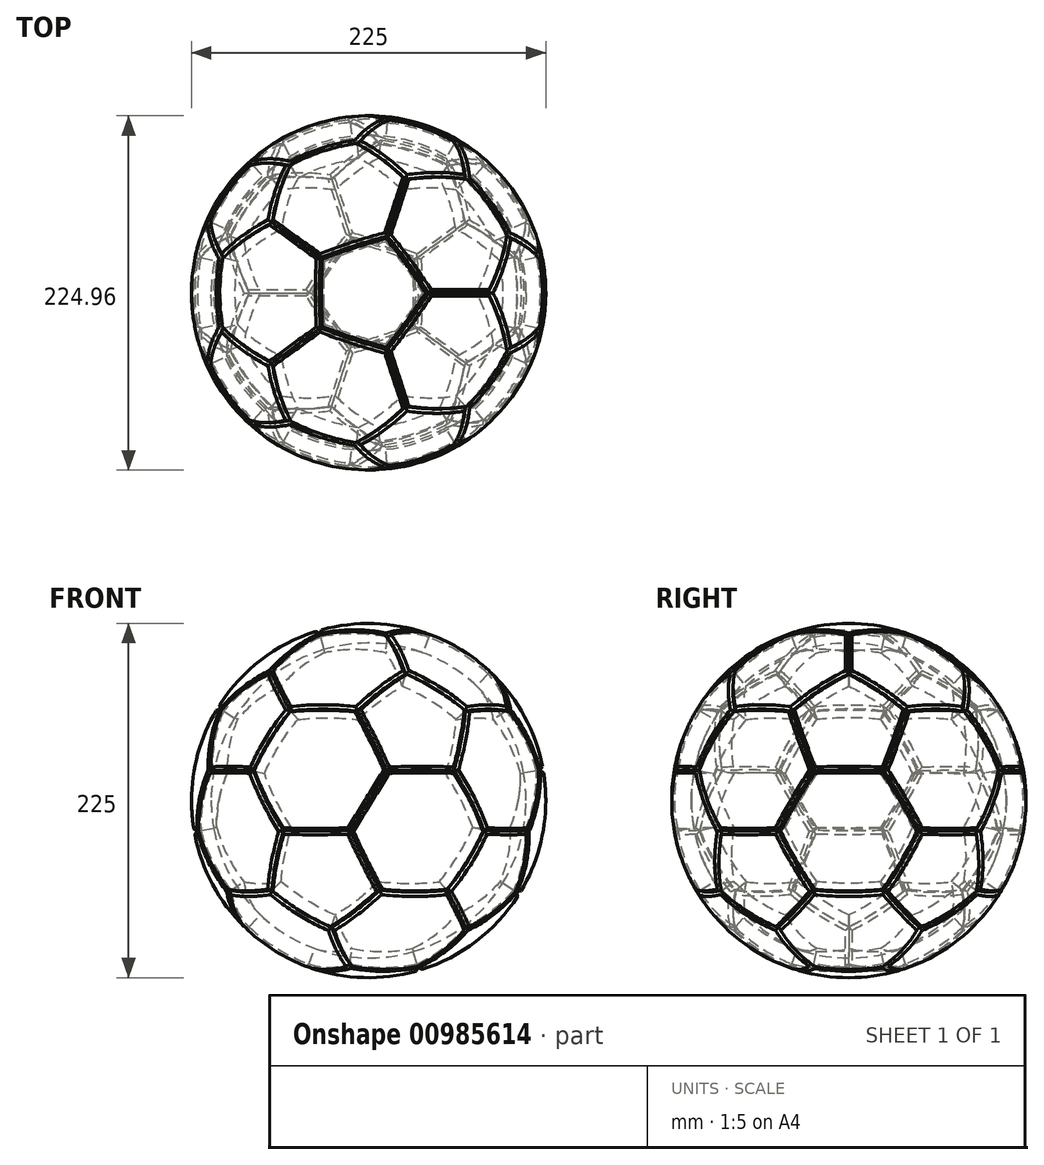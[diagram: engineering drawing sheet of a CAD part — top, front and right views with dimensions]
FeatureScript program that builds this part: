
annotation { "Feature Type Name" : "Feature", "Feature Type Description" : "" }
export const myFeature = defineFeature(function(context is Context, id is Id, definition is map)
    precondition{}
    {
        {
            var Q0;
            Q0=qCreatedBy(makeId("Top.planeOp"),FACE);
            var sketch = newSketch(context, id + "F0", { "sketchPlane" : qUnion([Q0])});
            skLineSegment(sketch, "E0.0", {"start": v(-13.14, 40.45) * mm, "end": v(34.4, 25) * mm});
            skLineSegment(sketch, "E0.1", {"start": v(34.4, 25) * mm, "end": v(34.4, -25) * mm});
            skLineSegment(sketch, "E0.2", {"start": v(34.4, -25) * mm, "end": v(-13.14, -40.45) * mm});
            skLineSegment(sketch, "E0.3", {"start": v(-13.14, -40.45) * mm, "end": v(-42.53, 0) * mm});
            skLineSegment(sketch, "E0.4", {"start": v(-42.53, 0) * mm, "end": v(-13.14, 40.45) * mm});
            skLineSegment(sketch, "E1", {"start": v(34.4, -25) * mm, "end": v(34.4, -50) * mm, "construction": true});
            skLineSegment(sketch, "E2", {"start": v(77.71, -50) * mm, "end": v(34.4, -50) * mm, "construction": true});
            skLineSegment(sketch, "E3", {"start": v(34.4, -25) * mm, "end": v(-27.84, 20.23) * mm, "construction": true});
            skLineSegment(sketch, "E4.MirrorCS", {"start": v(34.4, -25) * mm, "end": v(58.19, -17.27) * mm, "construction": true});
            skLineSegment(sketch, "E5.MirrorCS", {"start": v(71.57, -58.46) * mm, "end": v(58.19, -17.27) * mm, "construction": true});
            skSolve(sketch);
        }
        {
            var Q0;
            Q0=sQuery(id+"F0.wireOp",VERTEX,"E1.end");
            var Q1;
            Q1=sQuery(id+"F0.wireOp",EDGE,"E1");
            cPlane(context, id + "F1", {"entities" : qUnion([Q0, Q1]), "cplaneType" : CPlaneType.LINE_POINT, "offset" : 25 * mm, "width" : 150 * mm, "height" : 150 * mm});
        }
        {
            var Q0;
            Q0=qCreatedBy(id+"F1.planeOp",FACE);
            var sketch = newSketch(context, id + "F2", { "sketchPlane" : qUnion([Q0])});
            skCircle(sketch, "E6", {"center": v(34.4, 0) * mm, "radius": 43.3 * mm});
            skSolve(sketch);
        }
        {
            var Q0;
            Q0=sQuery(id+"F0.wireOp",VERTEX,"E4.MirrorCS.end");
            var Q1;
            Q1=sQuery(id+"F0.wireOp",EDGE,"E4.MirrorCS");
            cPlane(context, id + "F3", {"entities" : qUnion([Q0, Q1]), "cplaneType" : CPlaneType.LINE_POINT, "offset" : 25 * mm, "width" : 150 * mm, "height" : 150 * mm});
        }
        {
            var Q0;
            Q0=qCreatedBy(id+"F3.planeOp",FACE);
            var sketch = newSketch(context, id + "F4", { "sketchPlane" : qUnion([Q0])});
            skCircle(sketch, "E7", {"center": v(-34.4, 0) * mm, "radius": 43.3 * mm});
            skSolve(sketch);
        }
        {
            var Q0;
            Q0=makeQuery(id+"F2.imprint","IMPRINT",FACE,{"disambiguationData":[TD([[makeQuery(id+"F2.imprint","IMPRINT",EDGE,{"derivedFrom":sQuery(id+"F2.wireOp",EDGE,"E6")}),1.0]])]});
            extrude(context, id + "F5", {"entities" : qUnion([Q0]), "depth" : 25 * mm, "offsetDistance" : 25 * mm});
        }
        {
            var Q0;
            Q0=makeQuery(id+"F4.imprint","IMPRINT",FACE,{"disambiguationData":[TD([[makeQuery(id+"F4.imprint","IMPRINT",EDGE,{"derivedFrom":sQuery(id+"F4.wireOp",EDGE,"E7")}),1.0]])]});
            extrude(context, id + "F6", {"entities" : qUnion([Q0]), "depth" : 25 * mm, "offsetDistance" : 25 * mm});
        }
        {
            var Q0;
            Q0=makeQuery(id+"F5.opExtrude","SWEPT_BODY",BODY,{"disambiguationData":[OSD([sQuery(id+"F2.wireOp",EDGE,"E6")])]});
            var Q1;
            Q1=makeQuery(id+"F6.opExtrude","SWEPT_BODY",BODY,{"disambiguationData":[OSD([sQuery(id+"F4.wireOp",EDGE,"E7")])]});
            booleanBodies(context, id + "F7", {"operationType" : BooleanOperationType.INTERSECTION, "tools" : qUnion([Q0, Q1])});
        }
        {
            var Q0;
            Q0=sQuery(id+"F0.wireOp",VERTEX,"E0.0.end");
            var Q1;
            Q1=sQuery(id+"F0.wireOp",VERTEX,"E0.1.end");
            var Q2;
            {var subQ0=sQuery(id+"F4.wireOp",EDGE,"E7");var subQ1=sQuery(id+"F2.wireOp",EDGE,"E6");Q2=makeQuery(id+"F7.opBoolean","INTERSECT",VERTEX,{"disambiguationData":[OD(1.0)],"derivedFrom":[makeQuery(id+"F5.opExtrude","SWEPT_FACE",FACE,{"disambiguationData":[OSD([subQ1])]}),makeQuery(id+"F5.opExtrude","CAP_FACE",FACE,{"disambiguationData":[OSD([subQ1])],"isStart":true}),makeQuery(id+"F6.opExtrude","SWEPT_FACE",FACE,{"disambiguationData":[OSD([subQ0])]}),makeQuery(id+"F6.opExtrude","CAP_FACE",FACE,{"disambiguationData":[OSD([subQ0])],"isStart":true})]});}
            cPlane(context, id + "F8", {"entities" : qUnion([Q0, Q1, Q2]), "cplaneType" : CPlaneType.THREE_POINT, "offset" : 25 * mm, "width" : 150 * mm, "height" : 150 * mm});
        }
        {
            var Q0;
            Q0=qCreatedBy(id+"F8.planeOp",FACE);
            var sketch = newSketch(context, id + "F9", { "sketchPlane" : qUnion([Q0])});
            skLineSegment(sketch, "E8.0", {"start": v(113.95, 25) * mm, "end": v(113.95, -25) * mm});
            skLineSegment(sketch, "E8.1", {"start": v(113.95, -25) * mm, "end": v(70.64, -50) * mm});
            skLineSegment(sketch, "E8.2", {"start": v(70.64, -50) * mm, "end": v(27.34, -25) * mm});
            skLineSegment(sketch, "E8.3", {"start": v(27.34, -25) * mm, "end": v(27.34, 25) * mm});
            skLineSegment(sketch, "E8.4", {"start": v(27.34, 25) * mm, "end": v(70.64, 50) * mm});
            skLineSegment(sketch, "E8.5", {"start": v(70.64, 50) * mm, "end": v(113.95, 25) * mm});
            skLineSegment(sketch, "E9", {"start": v(70.64, 0) * mm, "end": v(27.34, -25) * mm, "construction": true});
            skSolve(sketch);
        }
        {
            var Q0;
            Q0=qCreatedBy(makeId("Front.planeOp"),FACE);
            var sketch = newSketch(context, id + "F10", { "sketchPlane" : qUnion([Q0])});
            skLineSegment(sketch, "E10", {"start": v(0, 0) * mm, "end": v(0, 116.37) * mm, "construction": true});
            skLineSegment(sketch, "E11", {"start": v(68.82, 26.29) * mm, "end": v(0, 116.37) * mm, "construction": true});
            skSolve(sketch);
        }
        {
            var Q0;
            Q0=makeQuery(id+"F0.imprint","IMPRINT",FACE,{"disambiguationData":[TD([[makeQuery(id+"F0.imprint","IMPRINT",EDGE,{"derivedFrom":sQuery(id+"F0.wireOp",EDGE,"E0.0")}),-1.0]])]});
            var Q1;
            Q1=sQuery(id+"F10.wireOp",VERTEX,"E10.end");
            loft(context, id + "F11", {"sheetProfilesArray" : [{ "sheetProfileEntities" : qUnion([Q0]) }, { "sheetProfileEntities" : qUnion([Q1]) }]});
        }
        {
            var Q1;
            Q1=makeQuery(id+"F9.imprint","IMPRINT",FACE,{"disambiguationData":[TD([[makeQuery(id+"F9.imprint","IMPRINT",EDGE,{"derivedFrom":sQuery(id+"F9.wireOp",EDGE,"E8.0")}),-1.0]])]});
            var Q2;
            Q2=sQuery(id+"F10.wireOp",VERTEX,"E10.end");
            loft(context, id + "F12", {"sheetProfilesArray" : [{ "sheetProfileEntities" : qUnion([Q1]) }, { "sheetProfileEntities" : qUnion([Q2]) }]});
        }
        {
            var Q0;
            Q0=makeQuery(id+"F12.opLoft","SWEPT_BODY",BODY,{"disambiguationData":[OSD([makeQuery(id+"F9.imprint","IMPRINT",FACE,{"disambiguationData":[TD([[makeQuery(id+"F9.imprint","IMPRINT",EDGE,{"derivedFrom":sQuery(id+"F9.wireOp",EDGE,"E8.0")}),-1.0]])]}),sQuery(id+"F10.wireOp",VERTEX,"E10.end")])]});
            var Q1;
            Q1=sQuery(id+"F10.wireOp",EDGE,"E10");
            circularPattern(context, id + "F13", {"entities" : qUnion([Q0]), "axis" : qUnion([Q1]), "angle" : 360 * degree, "instanceCount" : 5, "equalSpace" : true});
        }
        {
            var Q0;
            Q0=makeQuery(id+"F12.opLoft","MID_CAP_EDGE",EDGE,{"disambiguationData":[OSD([sQuery(id+"F9.wireOp",EDGE,"E8.3"),sQuery(id+"F9.wireOp",EDGE,"E8.4"),sQuery(id+"F9.wireOp",EDGE,"E8.5")])],"capPos":0.0});
            cPoint(context, id + "F14", {"entities" : qUnion([Q0]), "parameter" : 0.5});
        }
        {
            var Q0;
            Q0=sQuery(id+"F10.wireOp",VERTEX,"E11.start");
            var Q1;
            Q1=qCreatedBy(id+"F14",VERTEX);
            var Q2;
            Q2=sQuery(id+"F10.wireOp",VERTEX,"E10.end");
            cPlane(context, id + "F15", {"entities" : qUnion([Q0, Q1, Q2]), "cplaneType" : CPlaneType.THREE_POINT, "offset" : 25 * mm, "width" : 150 * mm, "height" : 150 * mm});
        }
        {
            var Q0;
            Q0=makeQuery(id+"F11.opLoft","SWEPT_BODY",BODY,{"disambiguationData":[OSD([makeQuery(id+"F0.imprint","IMPRINT",FACE,{"disambiguationData":[TD([[makeQuery(id+"F0.imprint","IMPRINT",EDGE,{"derivedFrom":sQuery(id+"F0.wireOp",EDGE,"E0.0")}),-1.0]])]}),sQuery(id+"F10.wireOp",VERTEX,"E10.end")])]});
            var Q1;
            Q1=qCreatedBy(id+"F15.planeOp",FACE);
            mirror(context, id + "F16", {"entities" : qUnion([Q0]), "mirrorPlane" : qUnion([Q1])});
        }
        {
            var Q0;
            Q0=makeQuery(id+"F16.opPattern","COPY",BODY,{"derivedFrom":makeQuery(id+"F11.opLoft","SWEPT_BODY",BODY,{"disambiguationData":[OSD([makeQuery(id+"F0.imprint","IMPRINT",FACE,{"disambiguationData":[TD([[makeQuery(id+"F0.imprint","IMPRINT",EDGE,{"derivedFrom":sQuery(id+"F0.wireOp",EDGE,"E0.0")}),-1.0]])]}),sQuery(id+"F10.wireOp",VERTEX,"E10.end")])]}),"instanceName":"1"});
            var Q1;
            Q1=sQuery(id+"F10.wireOp",EDGE,"E10");
            circularPattern(context, id + "F17", {"entities" : qUnion([Q0]), "axis" : qUnion([Q1]), "angle" : 360 * degree, "instanceCount" : 5, "equalSpace" : true});
        }
        {
            var Q0;
            Q0=makeQuery(id+"F12.opLoft","SWEPT_BODY",BODY,{"disambiguationData":[OSD([makeQuery(id+"F9.imprint","IMPRINT",FACE,{"disambiguationData":[TD([[makeQuery(id+"F9.imprint","IMPRINT",EDGE,{"derivedFrom":sQuery(id+"F9.wireOp",EDGE,"E8.0")}),-1.0]])]}),sQuery(id+"F10.wireOp",VERTEX,"E10.end")])]});
            var Q1;
            Q1=makeQuery(id+"F12.opLoft","SWEPT_FACE",FACE,{"disambiguationData":[OSD([sQuery(id+"F9.wireOp",EDGE,"E8.0"),sQuery(id+"F9.wireOp",EDGE,"E8.1"),sQuery(id+"F9.wireOp",EDGE,"E8.5")])]});
            mirror(context, id + "F18", {"entities" : qUnion([Q0]), "mirrorPlane" : qUnion([Q1])});
        }
        {
            var Q0;
            Q0=makeQuery(id+"F18.opPattern","COPY",BODY,{"derivedFrom":makeQuery(id+"F12.opLoft","SWEPT_BODY",BODY,{"disambiguationData":[OSD([makeQuery(id+"F9.imprint","IMPRINT",FACE,{"disambiguationData":[TD([[makeQuery(id+"F9.imprint","IMPRINT",EDGE,{"derivedFrom":sQuery(id+"F9.wireOp",EDGE,"E8.0")}),-1.0]])]}),sQuery(id+"F10.wireOp",VERTEX,"E10.end")])]}),"instanceName":"1"});
            var Q1;
            Q1=sQuery(id+"F10.wireOp",EDGE,"E10");
            circularPattern(context, id + "F19", {"entities" : qUnion([Q0]), "axis" : qUnion([Q1]), "angle" : 360 * degree, "instanceCount" : 5, "equalSpace" : true});
        }
        {
            var Q0;
            Q0=makeQuery(id+"F17.opPattern","COPY",EDGE,{"derivedFrom":makeQuery(id+"F16.opPattern","COPY",EDGE,{"derivedFrom":makeQuery(id+"F11.opLoft","MID_CAP_EDGE",EDGE,{"disambiguationData":[OSD([sQuery(id+"F0.wireOp",EDGE,"E0.0"),sQuery(id+"F0.wireOp",EDGE,"E0.3"),sQuery(id+"F0.wireOp",EDGE,"E0.4")])],"capPos":0.0}),"instanceName":"1"}),"instanceName":"1"});
            cPoint(context, id + "F20", {"entities" : qUnion([Q0]), "parameter" : 0.5});
        }
        {
            var Q0;
            Q0=makeQuery(id+"F19.opPattern","COPY",VERTEX,{"derivedFrom":makeQuery(id+"F18.opPattern","COPY",VERTEX,{"derivedFrom":makeQuery(id+"F12.opLoft","MID_CAP_VERTEX",VERTEX,{"disambiguationData":[OSD([sQuery(id+"F9.wireOp",EDGE,"E8.3"),sQuery(id+"F9.wireOp",EDGE,"E8.4")])],"capPos":0.0}),"instanceName":"1"}),"instanceName":"1"});
            var Q1;
            Q1=makeQuery(id+"F18.opPattern","COPY",VERTEX,{"derivedFrom":makeQuery(id+"F12.opLoft","MID_CAP_VERTEX",VERTEX,{"disambiguationData":[OSD([sQuery(id+"F9.wireOp",EDGE,"E8.2"),sQuery(id+"F9.wireOp",EDGE,"E8.3")])],"capPos":0.0}),"instanceName":"1"});
            var Q2;
            Q2=qCreatedBy(id+"F20",VERTEX);
            cPlane(context, id + "F21", {"entities" : qUnion([Q0, Q1, Q2]), "cplaneType" : CPlaneType.THREE_POINT, "offset" : 25 * mm, "width" : 150 * mm, "height" : 150 * mm});
        }
        {
            var Q0;
            Q0=qCreatedBy(id+"F21.planeOp",FACE);
            var sketch = newSketch(context, id + "F22", { "sketchPlane" : qUnion([Q0])});
            skLineSegment(sketch, "E12.0", {"start": v(34.36, 66.98) * mm, "end": v(-15.18, 73.73) * mm});
            skLineSegment(sketch, "E12.1", {"start": v(-15.18, 73.73) * mm, "end": v(-34.1, 120.01) * mm});
            skLineSegment(sketch, "E12.2", {"start": v(-34.1, 120.01) * mm, "end": v(-3.49, 159.54) * mm});
            skLineSegment(sketch, "E12.3", {"start": v(-3.49, 159.54) * mm, "end": v(46.06, 152.79) * mm});
            skLineSegment(sketch, "E12.4", {"start": v(46.06, 152.79) * mm, "end": v(64.98, 106.5) * mm});
            skLineSegment(sketch, "E12.5", {"start": v(64.98, 106.5) * mm, "end": v(34.36, 66.98) * mm});
            skSolve(sketch);
        }
        {
            var Q0;
            Q0=makeQuery(id+"F22.imprint","IMPRINT",FACE,{"disambiguationData":[TD([[makeQuery(id+"F22.imprint","IMPRINT",EDGE,{"derivedFrom":sQuery(id+"F22.wireOp",EDGE,"E12.0")}),-1.0]])]});
            var Q1;
            Q1=sQuery(id+"F10.wireOp",VERTEX,"E10.end");
            loft(context, id + "F23", {"sheetProfilesArray" : [{ "sheetProfileEntities" : qUnion([Q0]) }, { "sheetProfileEntities" : qUnion([Q1]) }]});
        }
        {
            var Q0;
            Q0=makeQuery(id+"F23.opLoft","SWEPT_BODY",BODY,{"disambiguationData":[OSD([sQuery(id+"F10.wireOp",VERTEX,"E10.end"),makeQuery(id+"F22.imprint","IMPRINT",FACE,{"disambiguationData":[TD([[makeQuery(id+"F22.imprint","IMPRINT",EDGE,{"derivedFrom":sQuery(id+"F22.wireOp",EDGE,"E12.0")}),-1.0]])]})])]});
            var Q1;
            Q1=sQuery(id+"F10.wireOp",EDGE,"E10");
            circularPattern(context, id + "F24", {"entities" : qUnion([Q0]), "axis" : qUnion([Q1]), "angle" : 360 * degree, "instanceCount" : 5, "equalSpace" : true});
        }
        {
            var Q0;
            Q0=makeQuery(id+"F19.opPattern","COPY",EDGE,{"derivedFrom":makeQuery(id+"F18.opPattern","COPY",EDGE,{"derivedFrom":makeQuery(id+"F12.opLoft","MID_CAP_EDGE",EDGE,{"disambiguationData":[OSD([sQuery(id+"F9.wireOp",EDGE,"E8.2"),sQuery(id+"F9.wireOp",EDGE,"E8.3"),sQuery(id+"F9.wireOp",EDGE,"E8.4")])],"capPos":0.0}),"instanceName":"1"}),"instanceName":"3"});
            cPoint(context, id + "F25", {"entities" : qUnion([Q0]), "parameter" : 0.5});
        }
        {
            var Q0;
            Q0=makeQuery(id+"F24.opPattern","COPY",VERTEX,{"derivedFrom":makeQuery(id+"F23.opLoft","MID_CAP_VERTEX",VERTEX,{"disambiguationData":[OSD([sQuery(id+"F22.wireOp",EDGE,"E12.2"),sQuery(id+"F22.wireOp",EDGE,"E12.3")])],"capPos":0.0}),"instanceName":"2"});
            var Q1;
            Q1=makeQuery(id+"F24.opPattern","COPY",VERTEX,{"derivedFrom":makeQuery(id+"F23.opLoft","MID_CAP_VERTEX",VERTEX,{"disambiguationData":[OSD([sQuery(id+"F22.wireOp",EDGE,"E12.3"),sQuery(id+"F22.wireOp",EDGE,"E12.4")])],"capPos":0.0}),"instanceName":"3"});
            var Q2;
            Q2=qCreatedBy(id+"F25",VERTEX);
            cPlane(context, id + "F26", {"entities" : qUnion([Q0, Q1, Q2]), "cplaneType" : CPlaneType.THREE_POINT, "offset" : 25 * mm, "width" : 150 * mm, "height" : 150 * mm});
        }
        {
            var Q0;
            Q0=qCreatedBy(id+"F26.planeOp",FACE);
            var sketch = newSketch(context, id + "F27", { "sketchPlane" : qUnion([Q0])});
            skLineSegment(sketch, "E13.0", {"start": v(2.25, 74) * mm, "end": v(-45.3, 58.54) * mm});
            skLineSegment(sketch, "E13.1", {"start": v(-45.3, 58.54) * mm, "end": v(-74.7, 99) * mm});
            skLineSegment(sketch, "E13.2", {"start": v(-74.7, 99) * mm, "end": v(-45.3, 139.44) * mm});
            skLineSegment(sketch, "E13.3", {"start": v(-45.3, 139.44) * mm, "end": v(2.25, 124) * mm});
            skLineSegment(sketch, "E13.4", {"start": v(2.25, 124) * mm, "end": v(2.25, 74) * mm});
            skSolve(sketch);
        }
        {
            var Q0;
            Q0=makeQuery(id+"F27.imprint","IMPRINT",FACE,{"disambiguationData":[TD([[makeQuery(id+"F27.imprint","IMPRINT",EDGE,{"derivedFrom":sQuery(id+"F27.wireOp",EDGE,"E13.0")}),-1.0]])]});
            var Q1;
            Q1=sQuery(id+"F10.wireOp",VERTEX,"E10.end");
            loft(context, id + "F28", {"sheetProfilesArray" : [{ "sheetProfileEntities" : qUnion([Q0]) }, { "sheetProfileEntities" : qUnion([Q1]) }]});
        }
        {
            var Q0;
            Q0=makeQuery(id+"F28.opLoft","SWEPT_BODY",BODY,{"disambiguationData":[OSD([sQuery(id+"F10.wireOp",VERTEX,"E10.end"),makeQuery(id+"F27.imprint","IMPRINT",FACE,{"disambiguationData":[TD([[makeQuery(id+"F27.imprint","IMPRINT",EDGE,{"derivedFrom":sQuery(id+"F27.wireOp",EDGE,"E13.0")}),-1.0]])]})])]});
            var Q1;
            Q1=sQuery(id+"F10.wireOp",EDGE,"E10");
            circularPattern(context, id + "F29", {"entities" : qUnion([Q0]), "axis" : qUnion([Q1]), "angle" : 360 * degree, "instanceCount" : 5, "equalSpace" : true});
        }
        {
            var Q0;
            Q0=makeQuery(id+"F23.opLoft","SWEPT_BODY",BODY,{"disambiguationData":[OSD([sQuery(id+"F10.wireOp",VERTEX,"E10.end"),makeQuery(id+"F22.imprint","IMPRINT",FACE,{"disambiguationData":[TD([[makeQuery(id+"F22.imprint","IMPRINT",EDGE,{"derivedFrom":sQuery(id+"F22.wireOp",EDGE,"E12.0")}),-1.0]])]})])]});
            var Q1;
            Q1=makeQuery(id+"F23.opLoft","SWEPT_FACE",FACE,{"disambiguationData":[OSD([sQuery(id+"F22.wireOp",EDGE,"E12.2"),sQuery(id+"F22.wireOp",EDGE,"E12.3"),sQuery(id+"F22.wireOp",EDGE,"E12.4")])]});
            mirror(context, id + "F30", {"entities" : qUnion([Q0]), "mirrorPlane" : qUnion([Q1])});
        }
        {
            var Q0;
            Q0=makeQuery(id+"F30.opPattern","COPY",BODY,{"derivedFrom":makeQuery(id+"F23.opLoft","SWEPT_BODY",BODY,{"disambiguationData":[OSD([sQuery(id+"F10.wireOp",VERTEX,"E10.end"),makeQuery(id+"F22.imprint","IMPRINT",FACE,{"disambiguationData":[TD([[makeQuery(id+"F22.imprint","IMPRINT",EDGE,{"derivedFrom":sQuery(id+"F22.wireOp",EDGE,"E12.0")}),-1.0]])]})])]}),"instanceName":"1"});
            var Q1;
            Q1=sQuery(id+"F10.wireOp",EDGE,"E10");
            circularPattern(context, id + "F31", {"entities" : qUnion([Q0]), "axis" : qUnion([Q1]), "angle" : 360 * degree, "instanceCount" : 5, "equalSpace" : true});
        }
        {
            var Q0;
            Q0=makeQuery(id+"F29.opPattern","COPY",EDGE,{"derivedFrom":makeQuery(id+"F28.opLoft","MID_CAP_EDGE",EDGE,{"disambiguationData":[OSD([sQuery(id+"F27.wireOp",EDGE,"E13.2"),sQuery(id+"F27.wireOp",EDGE,"E13.3"),sQuery(id+"F27.wireOp",EDGE,"E13.4")])],"capPos":0.0}),"instanceName":"4"});
            cPoint(context, id + "F32", {"entities" : qUnion([Q0]), "parameter" : 0.5});
        }
        {
            var Q0;
            Q0=makeQuery(id+"F31.opPattern","COPY",EDGE,{"derivedFrom":makeQuery(id+"F30.opPattern","COPY",EDGE,{"derivedFrom":makeQuery(id+"F23.opLoft","MID_CAP_EDGE",EDGE,{"disambiguationData":[OSD([sQuery(id+"F22.wireOp",EDGE,"E12.0"),sQuery(id+"F22.wireOp",EDGE,"E12.1"),sQuery(id+"F22.wireOp",EDGE,"E12.2")])],"capPos":0.0}),"instanceName":"1"}),"instanceName":"2"});
            cPoint(context, id + "F33", {"entities" : qUnion([Q0]), "parameter" : 0.5});
        }
        {
            var Q0;
            Q0=makeQuery(id+"F29.opPattern","COPY",EDGE,{"derivedFrom":makeQuery(id+"F28.opLoft","MID_CAP_EDGE",EDGE,{"disambiguationData":[OSD([sQuery(id+"F27.wireOp",EDGE,"E13.1"),sQuery(id+"F27.wireOp",EDGE,"E13.2"),sQuery(id+"F27.wireOp",EDGE,"E13.3")])],"capPos":0.0}),"instanceName":"1"});
            cPoint(context, id + "F34", {"entities" : qUnion([Q0]), "parameter" : 0.5});
        }
        {
            var Q0;
            Q0=qCreatedBy(id+"F32",VERTEX);
            var Q1;
            Q1=qCreatedBy(id+"F33",VERTEX);
            var Q2;
            Q2=qCreatedBy(id+"F34",VERTEX);
            cPlane(context, id + "F35", {"entities" : qUnion([Q0, Q1, Q2]), "cplaneType" : CPlaneType.THREE_POINT, "offset" : 25 * mm, "width" : 150 * mm, "height" : 150 * mm});
        }
        {
            var Q0;
            Q0=makeQuery(id+"F28.opLoft","SWEPT_BODY",BODY,{"disambiguationData":[OSD([sQuery(id+"F10.wireOp",VERTEX,"E10.end"),makeQuery(id+"F27.imprint","IMPRINT",FACE,{"disambiguationData":[TD([[makeQuery(id+"F27.imprint","IMPRINT",EDGE,{"derivedFrom":sQuery(id+"F27.wireOp",EDGE,"E13.0")}),-1.0]])]})])]});
            var Q1;
            Q1=qCreatedBy(id+"F35.planeOp",FACE);
            mirror(context, id + "F36", {"entities" : qUnion([Q0]), "mirrorPlane" : qUnion([Q1])});
        }
        {
            var Q0;
            Q0=makeQuery(id+"F7.opBoolean","INTERSECT",BODY,{"derivedFrom":[makeQuery(id+"F5.opExtrude","SWEPT_BODY",BODY,{"disambiguationData":[OSD([sQuery(id+"F2.wireOp",EDGE,"E6")])]}),makeQuery(id+"F6.opExtrude","SWEPT_BODY",BODY,{"disambiguationData":[OSD([sQuery(id+"F4.wireOp",EDGE,"E7")])]})]});
            deleteBodies(context, id + "F37", {"entities" : qUnion([Q0])});
        }
        {
            var Q0;
            Q0=sQuery(id+"F10.wireOp",EDGE,"E10");
            var Q1;
            Q1=sQuery(id+"F10.wireOp",VERTEX,"E10.end");
            cPlane(context, id + "F38", {"entities" : qUnion([Q0, Q1]), "cplaneType" : CPlaneType.LINE_POINT, "offset" : 25 * mm, "width" : 150 * mm, "height" : 150 * mm});
        }
        {
            var Q0;
            Q0=qCreatedBy(id+"F38.planeOp",FACE);
            var sketch = newSketch(context, id + "F39", { "sketchPlane" : qUnion([Q0])});
            skArc(sketch, "E14", {"start": v(100, 0) * mm, "mid": v(0, 100) * mm, "end": v(-100, 0) * mm});
            skLineSegment(sketch, "E15", {"start": v(100, 0) * mm, "end": v(-100, 0) * mm});
            skSolve(sketch);
        }
        {
            var Q0;
            Q0=qSketchRegion(id+"F39",true);
            var Q1;
            Q1=sQuery(id+"F39.wireOp",EDGE,"E15");
            revolve(context, id + "F40", {"operationType" : NewBodyOperationType.REMOVE, "surfaceOperationType" : NewSurfaceOperationType.NEW, "entities" : qUnion([Q0]), "axis" : qUnion([Q1]), "revolveType" : RevolveType.FULL, "oppositeDirection" : true});
        }
        {
            var Q0;
            Q0=qCreatedBy(id+"F38.planeOp",FACE);
            var sketch = newSketch(context, id + "F41", { "sketchPlane" : qUnion([Q0])});
            skArc(sketch, "E16", {"start": v(112.5, 0) * mm, "mid": v(0, 112.5) * mm, "end": v(-112.5, 0) * mm});
            skLineSegment(sketch, "E17", {"start": v(112.5, 0) * mm, "end": v(125, 0) * mm});
            skArc(sketch, "E18", {"start": v(125, 0) * mm, "mid": v(0, 125) * mm, "end": v(-125, 0) * mm});
            skLineSegment(sketch, "E19.trimOffspring", {"start": v(-125, 0) * mm, "end": v(-112.5, 0) * mm});
            skSolve(sketch);
        }
        {
            var Q0;
            Q0=makeQuery(id+"F41.imprint","IMPRINT",FACE,{"disambiguationData":[TD([[makeQuery(id+"F41.imprint","IMPRINT",EDGE,{"derivedFrom":sQuery(id+"F41.wireOp",EDGE,"E16")}),-1.0]])]});
            var Q1;
            Q1=sQuery(id+"F41.wireOp",EDGE,"E17");
            revolve(context, id + "F42", {"operationType" : NewBodyOperationType.REMOVE, "surfaceOperationType" : NewSurfaceOperationType.NEW, "entities" : qUnion([Q0]), "axis" : qUnion([Q1]), "revolveType" : RevolveType.FULL, "oppositeDirection" : true});
        }
        {
            var Q0;
            {var subQ2=sQuery(id+"F22.wireOp",EDGE,"E12.1");var subQ3=sQuery(id+"F22.wireOp",EDGE,"E12.0");var subQ4=sQuery(id+"F22.wireOp",EDGE,"E12.5");Q0=makeQuery(id+"F42.boolean.opBoolean","COPY",FACE,{"disambiguationData":[TD([makeQuery(id+"F31.opPattern","COPY",FACE,{"derivedFrom":makeQuery(id+"F30.opPattern","COPY",FACE,{"derivedFrom":makeQuery(id+"F23.opLoft","SWEPT_FACE",FACE,{"disambiguationData":[OSD([subQ3,subQ2,subQ4])]}),"instanceName":"1"}),"instanceName":"3"})])],"derivedFrom":makeQuery(id+"F42.opRevolve","SWEPT_FACE",FACE,{"disambiguationData":[OSD([sQuery(id+"F41.wireOp",EDGE,"E16")])]})});}
            var Q1;
            {var subQ2=sQuery(id+"F22.wireOp",EDGE,"E12.1");var subQ3=sQuery(id+"F22.wireOp",EDGE,"E12.0");var subQ4=sQuery(id+"F22.wireOp",EDGE,"E12.5");Q1=makeQuery(id+"F42.boolean.opBoolean","COPY",FACE,{"disambiguationData":[TD([makeQuery(id+"F31.opPattern","COPY",FACE,{"derivedFrom":makeQuery(id+"F30.opPattern","COPY",FACE,{"derivedFrom":makeQuery(id+"F23.opLoft","SWEPT_FACE",FACE,{"disambiguationData":[OSD([subQ3,subQ2,subQ4])]}),"instanceName":"1"}),"instanceName":"4"})])],"derivedFrom":makeQuery(id+"F42.opRevolve","SWEPT_FACE",FACE,{"disambiguationData":[OSD([sQuery(id+"F41.wireOp",EDGE,"E16")])]})});}
            var Q2;
            {var subQ2=sQuery(id+"F27.wireOp",EDGE,"E13.1");var subQ3=sQuery(id+"F27.wireOp",EDGE,"E13.0");var subQ4=sQuery(id+"F27.wireOp",EDGE,"E13.4");Q2=makeQuery(id+"F42.boolean.opBoolean","COPY",FACE,{"disambiguationData":[TD([makeQuery(id+"F28.opLoft","SWEPT_FACE",FACE,{"disambiguationData":[OSD([subQ3,subQ2,subQ4])]})])],"derivedFrom":makeQuery(id+"F42.opRevolve","SWEPT_FACE",FACE,{"disambiguationData":[OSD([sQuery(id+"F41.wireOp",EDGE,"E16")])]})});}
            var Q3;
            {var subQ2=sQuery(id+"F22.wireOp",EDGE,"E12.1");var subQ3=sQuery(id+"F22.wireOp",EDGE,"E12.0");var subQ4=sQuery(id+"F22.wireOp",EDGE,"E12.5");Q3=makeQuery(id+"F42.boolean.opBoolean","COPY",FACE,{"disambiguationData":[TD([makeQuery(id+"F24.opPattern","COPY",FACE,{"derivedFrom":makeQuery(id+"F23.opLoft","SWEPT_FACE",FACE,{"disambiguationData":[OSD([subQ3,subQ2,subQ4])]}),"instanceName":"3"})])],"derivedFrom":makeQuery(id+"F42.opRevolve","SWEPT_FACE",FACE,{"disambiguationData":[OSD([sQuery(id+"F41.wireOp",EDGE,"E16")])]})});}
            var Q4;
            {var subQ2=sQuery(id+"F9.wireOp",EDGE,"E8.1");var subQ3=sQuery(id+"F9.wireOp",EDGE,"E8.0");var subQ4=sQuery(id+"F9.wireOp",EDGE,"E8.5");Q4=makeQuery(id+"F42.boolean.opBoolean","COPY",FACE,{"disambiguationData":[TD([makeQuery(id+"F19.opPattern","COPY",FACE,{"derivedFrom":makeQuery(id+"F18.opPattern","COPY",FACE,{"derivedFrom":makeQuery(id+"F12.opLoft","SWEPT_FACE",FACE,{"disambiguationData":[OSD([subQ3,subQ2,subQ4])]}),"instanceName":"1"}),"instanceName":"4"})])],"derivedFrom":makeQuery(id+"F42.opRevolve","SWEPT_FACE",FACE,{"disambiguationData":[OSD([sQuery(id+"F41.wireOp",EDGE,"E16")])]})});}
            var Q5;
            {var subQ2=sQuery(id+"F9.wireOp",EDGE,"E8.1");var subQ3=sQuery(id+"F9.wireOp",EDGE,"E8.0");var subQ4=sQuery(id+"F9.wireOp",EDGE,"E8.5");Q5=makeQuery(id+"F42.boolean.opBoolean","COPY",FACE,{"disambiguationData":[TD([makeQuery(id+"F19.opPattern","COPY",FACE,{"derivedFrom":makeQuery(id+"F18.opPattern","COPY",FACE,{"derivedFrom":makeQuery(id+"F12.opLoft","SWEPT_FACE",FACE,{"disambiguationData":[OSD([subQ3,subQ2,subQ4])]}),"instanceName":"1"}),"instanceName":"3"})])],"derivedFrom":makeQuery(id+"F42.opRevolve","SWEPT_FACE",FACE,{"disambiguationData":[OSD([sQuery(id+"F41.wireOp",EDGE,"E16")])]})});}
            var Q6;
            {var subQ2=sQuery(id+"F27.wireOp",EDGE,"E13.1");var subQ3=sQuery(id+"F27.wireOp",EDGE,"E13.0");var subQ4=sQuery(id+"F27.wireOp",EDGE,"E13.4");Q6=makeQuery(id+"F42.boolean.opBoolean","COPY",FACE,{"disambiguationData":[TD([makeQuery(id+"F29.opPattern","COPY",FACE,{"derivedFrom":makeQuery(id+"F28.opLoft","SWEPT_FACE",FACE,{"disambiguationData":[OSD([subQ3,subQ2,subQ4])]}),"instanceName":"1"})])],"derivedFrom":makeQuery(id+"F42.opRevolve","SWEPT_FACE",FACE,{"disambiguationData":[OSD([sQuery(id+"F41.wireOp",EDGE,"E16")])]})});}
            var Q7;
            {var subQ2=sQuery(id+"F22.wireOp",EDGE,"E12.1");var subQ3=sQuery(id+"F22.wireOp",EDGE,"E12.0");var subQ4=sQuery(id+"F22.wireOp",EDGE,"E12.5");Q7=makeQuery(id+"F42.boolean.opBoolean","COPY",FACE,{"disambiguationData":[TD([makeQuery(id+"F31.opPattern","COPY",FACE,{"derivedFrom":makeQuery(id+"F30.opPattern","COPY",FACE,{"derivedFrom":makeQuery(id+"F23.opLoft","SWEPT_FACE",FACE,{"disambiguationData":[OSD([subQ3,subQ2,subQ4])]}),"instanceName":"1"}),"instanceName":"2"})])],"derivedFrom":makeQuery(id+"F42.opRevolve","SWEPT_FACE",FACE,{"disambiguationData":[OSD([sQuery(id+"F41.wireOp",EDGE,"E16")])]})});}
            var Q8;
            {var subQ2=sQuery(id+"F27.wireOp",EDGE,"E13.1");var subQ3=sQuery(id+"F27.wireOp",EDGE,"E13.0");var subQ4=sQuery(id+"F27.wireOp",EDGE,"E13.4");Q8=makeQuery(id+"F42.boolean.opBoolean","COPY",FACE,{"disambiguationData":[TD([makeQuery(id+"F36.opPattern","COPY",FACE,{"derivedFrom":makeQuery(id+"F28.opLoft","SWEPT_FACE",FACE,{"disambiguationData":[OSD([subQ3,subQ2,subQ4])]}),"instanceName":"1"})])],"derivedFrom":makeQuery(id+"F42.opRevolve","SWEPT_FACE",FACE,{"disambiguationData":[OSD([sQuery(id+"F41.wireOp",EDGE,"E16")])]})});}
            var Q9;
            {var subQ2=sQuery(id+"F22.wireOp",EDGE,"E12.1");var subQ3=sQuery(id+"F22.wireOp",EDGE,"E12.0");var subQ4=sQuery(id+"F22.wireOp",EDGE,"E12.5");Q9=makeQuery(id+"F42.boolean.opBoolean","COPY",FACE,{"disambiguationData":[TD([makeQuery(id+"F24.opPattern","COPY",FACE,{"derivedFrom":makeQuery(id+"F23.opLoft","SWEPT_FACE",FACE,{"disambiguationData":[OSD([subQ3,subQ2,subQ4])]}),"instanceName":"2"})])],"derivedFrom":makeQuery(id+"F42.opRevolve","SWEPT_FACE",FACE,{"disambiguationData":[OSD([sQuery(id+"F41.wireOp",EDGE,"E16")])]})});}
            var Q10;
            {var subQ2=sQuery(id+"F27.wireOp",EDGE,"E13.1");var subQ3=sQuery(id+"F27.wireOp",EDGE,"E13.0");var subQ4=sQuery(id+"F27.wireOp",EDGE,"E13.4");Q10=makeQuery(id+"F42.boolean.opBoolean","COPY",FACE,{"disambiguationData":[TD([makeQuery(id+"F29.opPattern","COPY",FACE,{"derivedFrom":makeQuery(id+"F28.opLoft","SWEPT_FACE",FACE,{"disambiguationData":[OSD([subQ3,subQ2,subQ4])]}),"instanceName":"4"})])],"derivedFrom":makeQuery(id+"F42.opRevolve","SWEPT_FACE",FACE,{"disambiguationData":[OSD([sQuery(id+"F41.wireOp",EDGE,"E16")])]})});}
            var Q11;
            {var subQ2=sQuery(id+"F9.wireOp",EDGE,"E8.1");var subQ3=sQuery(id+"F9.wireOp",EDGE,"E8.0");var subQ4=sQuery(id+"F9.wireOp",EDGE,"E8.5");Q11=makeQuery(id+"F42.boolean.opBoolean","COPY",FACE,{"disambiguationData":[TD([makeQuery(id+"F19.opPattern","COPY",FACE,{"derivedFrom":makeQuery(id+"F18.opPattern","COPY",FACE,{"derivedFrom":makeQuery(id+"F12.opLoft","SWEPT_FACE",FACE,{"disambiguationData":[OSD([subQ3,subQ2,subQ4])]}),"instanceName":"1"}),"instanceName":"2"})])],"derivedFrom":makeQuery(id+"F42.opRevolve","SWEPT_FACE",FACE,{"disambiguationData":[OSD([sQuery(id+"F41.wireOp",EDGE,"E16")])]})});}
            var Q12;
            {var subQ2=sQuery(id+"F0.wireOp",EDGE,"E0.1");var subQ3=sQuery(id+"F0.wireOp",EDGE,"E0.0");var subQ4=sQuery(id+"F0.wireOp",EDGE,"E0.4");Q12=makeQuery(id+"F42.boolean.opBoolean","COPY",FACE,{"disambiguationData":[TD([makeQuery(id+"F17.opPattern","COPY",FACE,{"derivedFrom":makeQuery(id+"F16.opPattern","COPY",FACE,{"derivedFrom":makeQuery(id+"F11.opLoft","SWEPT_FACE",FACE,{"disambiguationData":[OSD([subQ3,subQ2,subQ4])]}),"instanceName":"1"}),"instanceName":"3"})])],"derivedFrom":makeQuery(id+"F42.opRevolve","SWEPT_FACE",FACE,{"disambiguationData":[OSD([sQuery(id+"F41.wireOp",EDGE,"E16")])]})});}
            var Q13;
            {var subQ2=sQuery(id+"F9.wireOp",EDGE,"E8.1");var subQ3=sQuery(id+"F9.wireOp",EDGE,"E8.0");var subQ4=sQuery(id+"F9.wireOp",EDGE,"E8.5");Q13=makeQuery(id+"F42.boolean.opBoolean","COPY",FACE,{"disambiguationData":[TD([makeQuery(id+"F13.opPattern","COPY",FACE,{"derivedFrom":makeQuery(id+"F12.opLoft","SWEPT_FACE",FACE,{"disambiguationData":[OSD([subQ3,subQ2,subQ4])]}),"instanceName":"3"})])],"derivedFrom":makeQuery(id+"F42.opRevolve","SWEPT_FACE",FACE,{"disambiguationData":[OSD([sQuery(id+"F41.wireOp",EDGE,"E16")])]})});}
            var Q14;
            {var subQ2=sQuery(id+"F9.wireOp",EDGE,"E8.1");var subQ3=sQuery(id+"F9.wireOp",EDGE,"E8.0");var subQ4=sQuery(id+"F9.wireOp",EDGE,"E8.5");Q14=makeQuery(id+"F42.boolean.opBoolean","COPY",FACE,{"disambiguationData":[TD([makeQuery(id+"F13.opPattern","COPY",FACE,{"derivedFrom":makeQuery(id+"F12.opLoft","SWEPT_FACE",FACE,{"disambiguationData":[OSD([subQ3,subQ2,subQ4])]}),"instanceName":"2"})])],"derivedFrom":makeQuery(id+"F42.opRevolve","SWEPT_FACE",FACE,{"disambiguationData":[OSD([sQuery(id+"F41.wireOp",EDGE,"E16")])]})});}
            var Q15;
            {var subQ2=sQuery(id+"F0.wireOp",EDGE,"E0.1");var subQ3=sQuery(id+"F0.wireOp",EDGE,"E0.0");var subQ4=sQuery(id+"F0.wireOp",EDGE,"E0.4");Q15=makeQuery(id+"F42.boolean.opBoolean","COPY",FACE,{"disambiguationData":[TD([makeQuery(id+"F11.opLoft","SWEPT_FACE",FACE,{"disambiguationData":[OSD([subQ3,subQ2,subQ4])]})])],"derivedFrom":makeQuery(id+"F42.opRevolve","SWEPT_FACE",FACE,{"disambiguationData":[OSD([sQuery(id+"F41.wireOp",EDGE,"E16")])]})});}
            var Q16;
            {var subQ2=sQuery(id+"F9.wireOp",EDGE,"E8.1");var subQ3=sQuery(id+"F9.wireOp",EDGE,"E8.0");var subQ4=sQuery(id+"F9.wireOp",EDGE,"E8.5");Q16=makeQuery(id+"F42.boolean.opBoolean","COPY",FACE,{"disambiguationData":[TD([makeQuery(id+"F13.opPattern","COPY",FACE,{"derivedFrom":makeQuery(id+"F12.opLoft","SWEPT_FACE",FACE,{"disambiguationData":[OSD([subQ3,subQ2,subQ4])]}),"instanceName":"4"})])],"derivedFrom":makeQuery(id+"F42.opRevolve","SWEPT_FACE",FACE,{"disambiguationData":[OSD([sQuery(id+"F41.wireOp",EDGE,"E16")])]})});}
            var Q17;
            {var subQ2=sQuery(id+"F9.wireOp",EDGE,"E8.1");var subQ3=sQuery(id+"F9.wireOp",EDGE,"E8.0");var subQ4=sQuery(id+"F9.wireOp",EDGE,"E8.5");Q17=makeQuery(id+"F42.boolean.opBoolean","COPY",FACE,{"disambiguationData":[TD([makeQuery(id+"F12.opLoft","SWEPT_FACE",FACE,{"disambiguationData":[OSD([subQ3,subQ2,subQ4])]})])],"derivedFrom":makeQuery(id+"F42.opRevolve","SWEPT_FACE",FACE,{"disambiguationData":[OSD([sQuery(id+"F41.wireOp",EDGE,"E16")])]})});}
            var Q18;
            {var subQ2=sQuery(id+"F9.wireOp",EDGE,"E8.1");var subQ3=sQuery(id+"F9.wireOp",EDGE,"E8.0");var subQ4=sQuery(id+"F9.wireOp",EDGE,"E8.5");Q18=makeQuery(id+"F42.boolean.opBoolean","COPY",FACE,{"disambiguationData":[TD([makeQuery(id+"F13.opPattern","COPY",FACE,{"derivedFrom":makeQuery(id+"F12.opLoft","SWEPT_FACE",FACE,{"disambiguationData":[OSD([subQ3,subQ2,subQ4])]}),"instanceName":"1"})])],"derivedFrom":makeQuery(id+"F42.opRevolve","SWEPT_FACE",FACE,{"disambiguationData":[OSD([sQuery(id+"F41.wireOp",EDGE,"E16")])]})});}
            var Q19;
            {var subQ2=sQuery(id+"F9.wireOp",EDGE,"E8.1");var subQ3=sQuery(id+"F9.wireOp",EDGE,"E8.0");var subQ4=sQuery(id+"F9.wireOp",EDGE,"E8.5");Q19=makeQuery(id+"F42.boolean.opBoolean","COPY",FACE,{"disambiguationData":[TD([makeQuery(id+"F19.opPattern","COPY",FACE,{"derivedFrom":makeQuery(id+"F18.opPattern","COPY",FACE,{"derivedFrom":makeQuery(id+"F12.opLoft","SWEPT_FACE",FACE,{"disambiguationData":[OSD([subQ3,subQ2,subQ4])]}),"instanceName":"1"}),"instanceName":"1"})])],"derivedFrom":makeQuery(id+"F42.opRevolve","SWEPT_FACE",FACE,{"disambiguationData":[OSD([sQuery(id+"F41.wireOp",EDGE,"E16")])]})});}
            var Q20;
            {var subQ2=sQuery(id+"F22.wireOp",EDGE,"E12.1");var subQ3=sQuery(id+"F22.wireOp",EDGE,"E12.0");var subQ4=sQuery(id+"F22.wireOp",EDGE,"E12.5");Q20=makeQuery(id+"F42.boolean.opBoolean","COPY",FACE,{"disambiguationData":[TD([makeQuery(id+"F30.opPattern","COPY",FACE,{"derivedFrom":makeQuery(id+"F23.opLoft","SWEPT_FACE",FACE,{"disambiguationData":[OSD([subQ3,subQ2,subQ4])]}),"instanceName":"1"})])],"derivedFrom":makeQuery(id+"F42.opRevolve","SWEPT_FACE",FACE,{"disambiguationData":[OSD([sQuery(id+"F41.wireOp",EDGE,"E16")])]})});}
            var Q21;
            {var subQ2=sQuery(id+"F22.wireOp",EDGE,"E12.1");var subQ3=sQuery(id+"F22.wireOp",EDGE,"E12.0");var subQ4=sQuery(id+"F22.wireOp",EDGE,"E12.5");Q21=makeQuery(id+"F42.boolean.opBoolean","COPY",FACE,{"disambiguationData":[TD([makeQuery(id+"F31.opPattern","COPY",FACE,{"derivedFrom":makeQuery(id+"F30.opPattern","COPY",FACE,{"derivedFrom":makeQuery(id+"F23.opLoft","SWEPT_FACE",FACE,{"disambiguationData":[OSD([subQ3,subQ2,subQ4])]}),"instanceName":"1"}),"instanceName":"1"})])],"derivedFrom":makeQuery(id+"F42.opRevolve","SWEPT_FACE",FACE,{"disambiguationData":[OSD([sQuery(id+"F41.wireOp",EDGE,"E16")])]})});}
            var Q22;
            {var subQ2=sQuery(id+"F22.wireOp",EDGE,"E12.1");var subQ3=sQuery(id+"F22.wireOp",EDGE,"E12.0");var subQ4=sQuery(id+"F22.wireOp",EDGE,"E12.5");Q22=makeQuery(id+"F42.boolean.opBoolean","COPY",FACE,{"disambiguationData":[TD([makeQuery(id+"F24.opPattern","COPY",FACE,{"derivedFrom":makeQuery(id+"F23.opLoft","SWEPT_FACE",FACE,{"disambiguationData":[OSD([subQ3,subQ2,subQ4])]}),"instanceName":"1"})])],"derivedFrom":makeQuery(id+"F42.opRevolve","SWEPT_FACE",FACE,{"disambiguationData":[OSD([sQuery(id+"F41.wireOp",EDGE,"E16")])]})});}
            var Q23;
            {var subQ2=sQuery(id+"F27.wireOp",EDGE,"E13.1");var subQ3=sQuery(id+"F27.wireOp",EDGE,"E13.0");var subQ4=sQuery(id+"F27.wireOp",EDGE,"E13.4");Q23=makeQuery(id+"F42.boolean.opBoolean","COPY",FACE,{"disambiguationData":[TD([makeQuery(id+"F29.opPattern","COPY",FACE,{"derivedFrom":makeQuery(id+"F28.opLoft","SWEPT_FACE",FACE,{"disambiguationData":[OSD([subQ3,subQ2,subQ4])]}),"instanceName":"3"})])],"derivedFrom":makeQuery(id+"F42.opRevolve","SWEPT_FACE",FACE,{"disambiguationData":[OSD([sQuery(id+"F41.wireOp",EDGE,"E16")])]})});}
            var Q24;
            {var subQ2=sQuery(id+"F22.wireOp",EDGE,"E12.1");var subQ3=sQuery(id+"F22.wireOp",EDGE,"E12.0");var subQ4=sQuery(id+"F22.wireOp",EDGE,"E12.5");Q24=makeQuery(id+"F42.boolean.opBoolean","COPY",FACE,{"disambiguationData":[TD([makeQuery(id+"F23.opLoft","SWEPT_FACE",FACE,{"disambiguationData":[OSD([subQ3,subQ2,subQ4])]})])],"derivedFrom":makeQuery(id+"F42.opRevolve","SWEPT_FACE",FACE,{"disambiguationData":[OSD([sQuery(id+"F41.wireOp",EDGE,"E16")])]})});}
            var Q25;
            {var subQ2=sQuery(id+"F9.wireOp",EDGE,"E8.1");var subQ3=sQuery(id+"F9.wireOp",EDGE,"E8.0");var subQ4=sQuery(id+"F9.wireOp",EDGE,"E8.5");Q25=makeQuery(id+"F42.boolean.opBoolean","COPY",FACE,{"disambiguationData":[TD([makeQuery(id+"F18.opPattern","COPY",FACE,{"derivedFrom":makeQuery(id+"F12.opLoft","SWEPT_FACE",FACE,{"disambiguationData":[OSD([subQ3,subQ2,subQ4])]}),"instanceName":"1"})])],"derivedFrom":makeQuery(id+"F42.opRevolve","SWEPT_FACE",FACE,{"disambiguationData":[OSD([sQuery(id+"F41.wireOp",EDGE,"E16")])]})});}
            var Q26;
            {var subQ2=sQuery(id+"F22.wireOp",EDGE,"E12.1");var subQ3=sQuery(id+"F22.wireOp",EDGE,"E12.0");var subQ4=sQuery(id+"F22.wireOp",EDGE,"E12.5");Q26=makeQuery(id+"F42.boolean.opBoolean","COPY",FACE,{"disambiguationData":[TD([makeQuery(id+"F24.opPattern","COPY",FACE,{"derivedFrom":makeQuery(id+"F23.opLoft","SWEPT_FACE",FACE,{"disambiguationData":[OSD([subQ3,subQ2,subQ4])]}),"instanceName":"4"})])],"derivedFrom":makeQuery(id+"F42.opRevolve","SWEPT_FACE",FACE,{"disambiguationData":[OSD([sQuery(id+"F41.wireOp",EDGE,"E16")])]})});}
            var Q27;
            {var subQ2=sQuery(id+"F27.wireOp",EDGE,"E13.1");var subQ3=sQuery(id+"F27.wireOp",EDGE,"E13.0");var subQ4=sQuery(id+"F27.wireOp",EDGE,"E13.4");Q27=makeQuery(id+"F42.boolean.opBoolean","COPY",FACE,{"disambiguationData":[TD([makeQuery(id+"F29.opPattern","COPY",FACE,{"derivedFrom":makeQuery(id+"F28.opLoft","SWEPT_FACE",FACE,{"disambiguationData":[OSD([subQ3,subQ2,subQ4])]}),"instanceName":"2"})])],"derivedFrom":makeQuery(id+"F42.opRevolve","SWEPT_FACE",FACE,{"disambiguationData":[OSD([sQuery(id+"F41.wireOp",EDGE,"E16")])]})});}
            var Q28;
            {var subQ2=sQuery(id+"F0.wireOp",EDGE,"E0.1");var subQ3=sQuery(id+"F0.wireOp",EDGE,"E0.0");var subQ4=sQuery(id+"F0.wireOp",EDGE,"E0.4");Q28=makeQuery(id+"F42.boolean.opBoolean","COPY",FACE,{"disambiguationData":[TD([makeQuery(id+"F17.opPattern","COPY",FACE,{"derivedFrom":makeQuery(id+"F16.opPattern","COPY",FACE,{"derivedFrom":makeQuery(id+"F11.opLoft","SWEPT_FACE",FACE,{"disambiguationData":[OSD([subQ3,subQ2,subQ4])]}),"instanceName":"1"}),"instanceName":"1"})])],"derivedFrom":makeQuery(id+"F42.opRevolve","SWEPT_FACE",FACE,{"disambiguationData":[OSD([sQuery(id+"F41.wireOp",EDGE,"E16")])]})});}
            var Q29;
            {var subQ2=sQuery(id+"F0.wireOp",EDGE,"E0.1");var subQ3=sQuery(id+"F0.wireOp",EDGE,"E0.0");var subQ4=sQuery(id+"F0.wireOp",EDGE,"E0.4");Q29=makeQuery(id+"F42.boolean.opBoolean","COPY",FACE,{"disambiguationData":[TD([makeQuery(id+"F17.opPattern","COPY",FACE,{"derivedFrom":makeQuery(id+"F16.opPattern","COPY",FACE,{"derivedFrom":makeQuery(id+"F11.opLoft","SWEPT_FACE",FACE,{"disambiguationData":[OSD([subQ3,subQ2,subQ4])]}),"instanceName":"1"}),"instanceName":"2"})])],"derivedFrom":makeQuery(id+"F42.opRevolve","SWEPT_FACE",FACE,{"disambiguationData":[OSD([sQuery(id+"F41.wireOp",EDGE,"E16")])]})});}
            var Q30;
            {var subQ2=sQuery(id+"F0.wireOp",EDGE,"E0.1");var subQ3=sQuery(id+"F0.wireOp",EDGE,"E0.0");var subQ4=sQuery(id+"F0.wireOp",EDGE,"E0.4");Q30=makeQuery(id+"F42.boolean.opBoolean","COPY",FACE,{"disambiguationData":[TD([makeQuery(id+"F16.opPattern","COPY",FACE,{"derivedFrom":makeQuery(id+"F11.opLoft","SWEPT_FACE",FACE,{"disambiguationData":[OSD([subQ3,subQ2,subQ4])]}),"instanceName":"1"})])],"derivedFrom":makeQuery(id+"F42.opRevolve","SWEPT_FACE",FACE,{"disambiguationData":[OSD([sQuery(id+"F41.wireOp",EDGE,"E16")])]})});}
            var Q31;
            {var subQ2=sQuery(id+"F0.wireOp",EDGE,"E0.1");var subQ3=sQuery(id+"F0.wireOp",EDGE,"E0.0");var subQ4=sQuery(id+"F0.wireOp",EDGE,"E0.4");Q31=makeQuery(id+"F42.boolean.opBoolean","COPY",FACE,{"disambiguationData":[TD([makeQuery(id+"F17.opPattern","COPY",FACE,{"derivedFrom":makeQuery(id+"F16.opPattern","COPY",FACE,{"derivedFrom":makeQuery(id+"F11.opLoft","SWEPT_FACE",FACE,{"disambiguationData":[OSD([subQ3,subQ2,subQ4])]}),"instanceName":"1"}),"instanceName":"4"})])],"derivedFrom":makeQuery(id+"F42.opRevolve","SWEPT_FACE",FACE,{"disambiguationData":[OSD([sQuery(id+"F41.wireOp",EDGE,"E16")])]})});}
            chamfer(context, id + "F43", {"entities" : qUnion([Q0, Q1, Q2, Q3, Q4, Q5, Q6, Q7, Q8, Q9, Q10, Q11, Q12, Q13, Q14, Q15, Q16, Q17, Q18, Q19, Q20, Q21, Q22, Q23, Q24, Q25, Q26, Q27, Q28, Q29, Q30, Q31]), "width" : 2 * mm, "tangentPropagation" : true});
        }
    });
